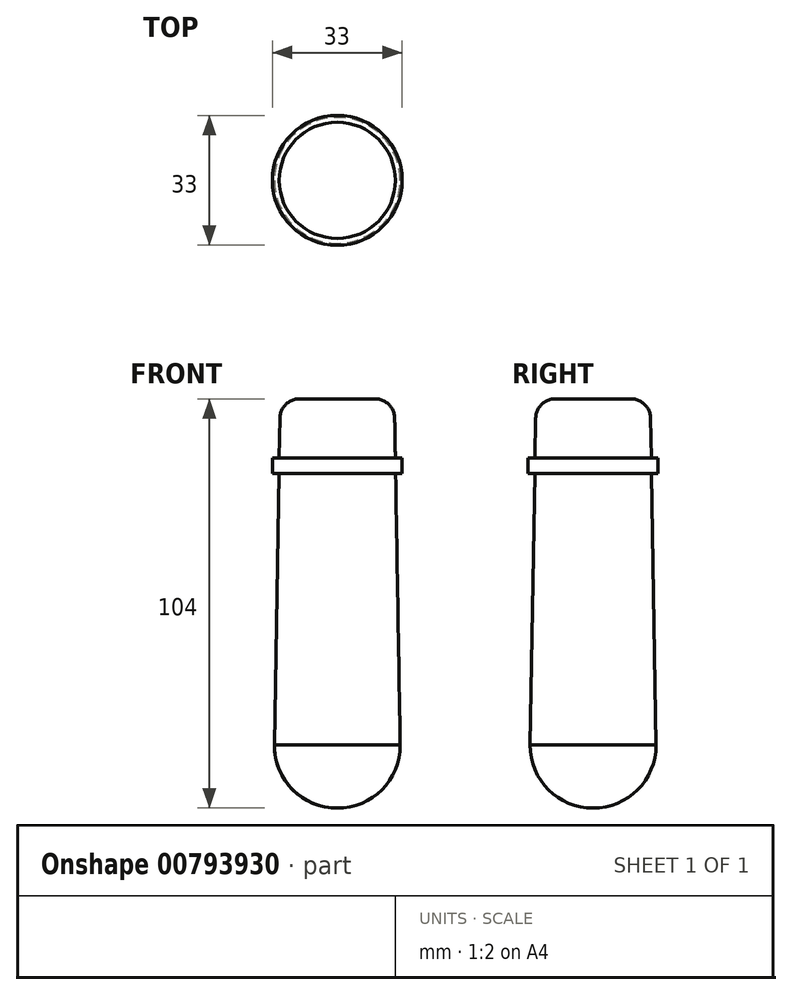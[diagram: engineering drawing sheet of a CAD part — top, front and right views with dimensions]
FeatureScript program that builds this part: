
annotation { "Feature Type Name" : "Feature", "Feature Type Description" : "" }
export const myFeature = defineFeature(function(context is Context, id is Id, definition is map)
    precondition{}
    {
        {
            var Q0;
            Q0=qCreatedBy(makeId("Front.planeOp"),FACE);
            var sketch = newSketch(context, id + "F0", { "sketchPlane" : qUnion([Q0])});
            skLineSegment(sketch, "E0", {"start": v(0, 43.76) * mm, "end": v(0, -60.24) * mm});
            skLineSegment(sketch, "E1", {"start": v(0, -44.24) * mm, "end": v(16, -44.24) * mm});
            skArc(sketch, "E2", {"start": v(16, -44.24) * mm, "mid": v(11.31, -55.56) * mm, "end": v(0, -60.24) * mm});
            skPoint(sketch, "E3", {"position": v(0, 24.76) * mm});
            skLineSegment(sketch, "E4", {"start": v(0, 43.76) * mm, "end": v(14.5, 43.76) * mm});
            skLineSegment(sketch, "E5", {"start": v(14.82, 24.76) * mm, "end": v(16.5, 24.76) * mm});
            skLineSegment(sketch, "E6", {"start": v(16.5, 24.76) * mm, "end": v(16.5, 28.76) * mm});
            skLineSegment(sketch, "E7", {"start": v(16.5, 28.76) * mm, "end": v(14.76, 28.76) * mm});
            skLineSegment(sketch, "E8", {"start": v(14.5, 43.76) * mm, "end": v(16, -44.24) * mm});
            skSolve(sketch);
        }
        {
            var Q0;
            Q0 = qSketchRegion(id + "F0", true);
            var Q1;
            Q1=sQuery(id+"F0.wireOp",EDGE,"E0");
            revolve(context, id + "F1", {"surfaceOperationType" : NewSurfaceOperationType.NEW, "entities" : qUnion([Q0]), "axis" : qUnion([Q1]), "revolveType" : RevolveType.FULL});
        }
        {
            var Q0;
            Q0=makeQuery(id+"F1.opRevolve","SWEPT_EDGE",EDGE,{"disambiguationData":[OSD([sQuery(id+"F0.wireOp",EDGE,"E4"),sQuery(id+"F0.wireOp",EDGE,"E8")])]});
            fillet(context, id + "F2", {"entities" : qUnion([Q0]), "radius" : 5 * mm, "tangentPropagation" : true, "allowEdgeOverflow" : false});
        }
    });
